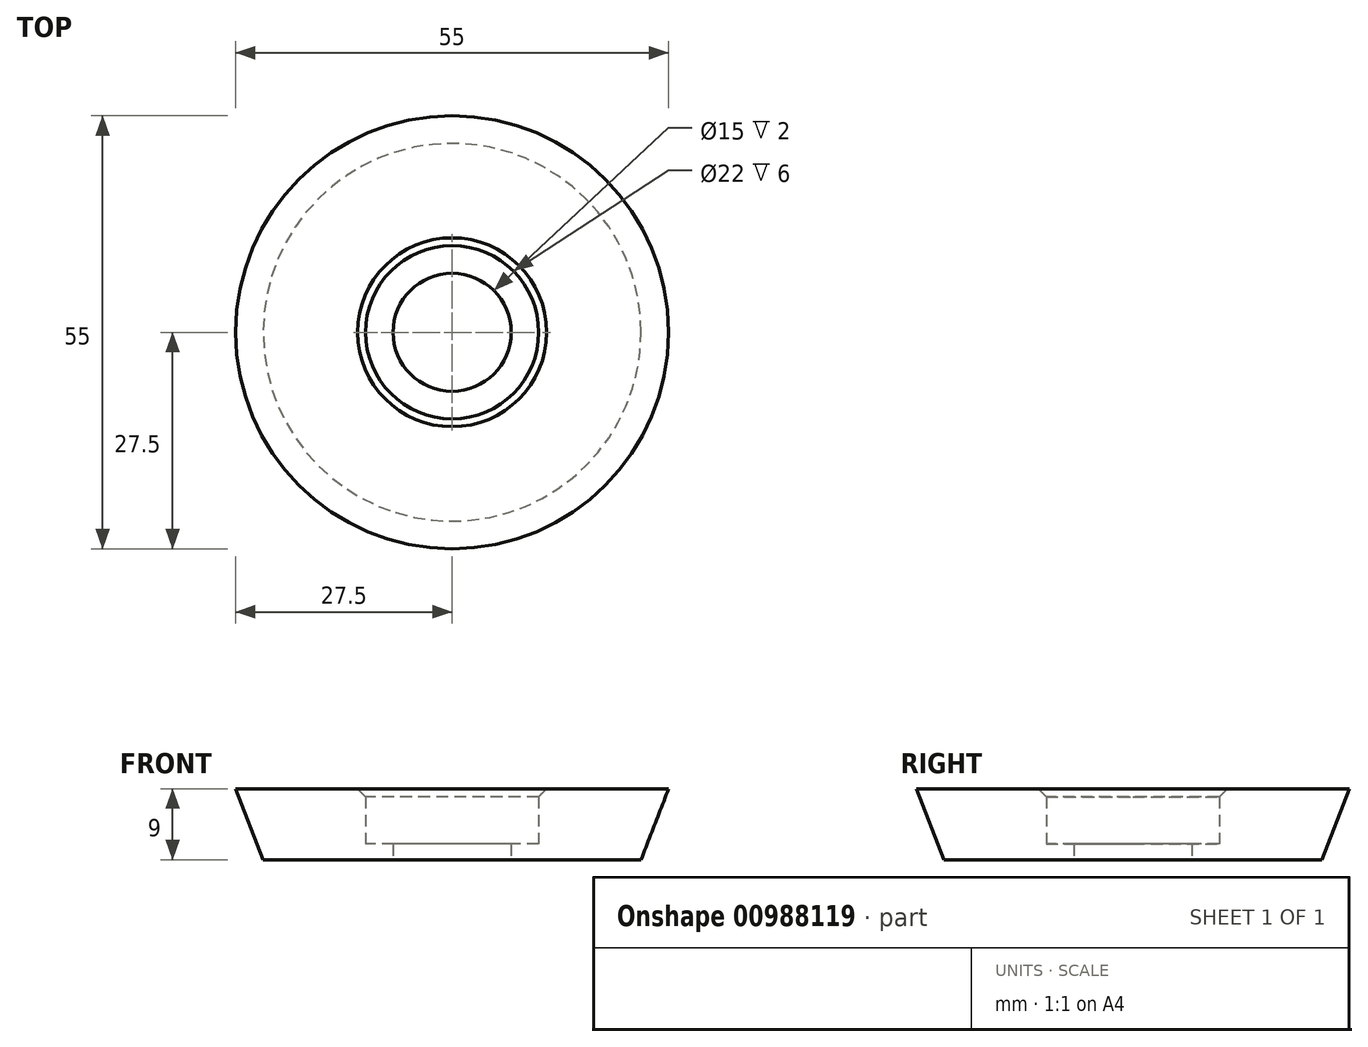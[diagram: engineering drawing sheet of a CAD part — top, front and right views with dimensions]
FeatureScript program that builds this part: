
annotation { "Feature Type Name" : "Feature", "Feature Type Description" : "" }
export const myFeature = defineFeature(function(context is Context, id is Id, definition is map)
    precondition{}
    {
        {
            var Q0;
            Q0=qCreatedBy(makeId("Top.planeOp"),FACE);
            var sketch = newSketch(context, id + "F0", { "sketchPlane" : qUnion([Q0])});
            skCircle(sketch, "E0", {"center": v(0, 0) * mm, "radius": 7.5 * mm});
            skCircle(sketch, "E1", {"center": v(0, 0) * mm, "radius": 27.5 * mm});
            skSolve(sketch);
        }
        {
            var Q0;
            Q0 = qSketchRegion(id + "F0", true);
            extrude(context, id + "F1", {"entities" : qUnion([Q0]), "depth" : 2 * mm, "offsetDistance" : 25 * mm});
        }
        {
            var Q0;
            Q0=makeQuery(id+"F1.opExtrude","CAP_FACE",FACE,{"disambiguationData":[OSD([sQuery(id+"F0.wireOp",EDGE,"E0"),sQuery(id+"F0.wireOp",EDGE,"E1")])],"isStart":false});
            var sketch = newSketch(context, id + "F2", { "sketchPlane" : qUnion([Q0])});
            skCircle(sketch, "E2", {"center": v(0, 0) * mm, "radius": 11 * mm});
            skCircle(sketch, "E3.0", {"center": v(0, 0) * mm, "radius": 27.5 * mm});
            skSolve(sketch);
        }
        {
            var Q0;
            Q0 = qSketchRegion(id + "F2", true);
            extrude(context, id + "F3", {"entities" : qUnion([Q0]), "operationType" : NewBodyOperationType.ADD, "depth" : 7 * mm, "offsetDistance" : 25 * mm});
        }
        {
            var Q0;
            Q0=makeQuery(id+"F1.opExtrude","CAP_EDGE",EDGE,{"disambiguationData":[OSD([sQuery(id+"F0.wireOp",EDGE,"E1")])],"isStart":true});
            chamfer(context, id + "F4", {"entities" : qUnion([Q0]), "chamferType" : ChamferType.TWO_OFFSETS, "width1" : 9 * mm, "oppositeDirection" : false, "width2" : 3.5 * mm, "tangentPropagation" : true});
        }
        {
            var Q0;
            Q0=makeQuery(id+"F3.opExtrude","CAP_EDGE",EDGE,{"disambiguationData":[OSD([sQuery(id+"F2.wireOp",EDGE,"E2")])],"isStart":false});
            chamfer(context, id + "F5", {"entities" : qUnion([Q0]), "width" : 1 * mm, "tangentPropagation" : true});
        }
    });
